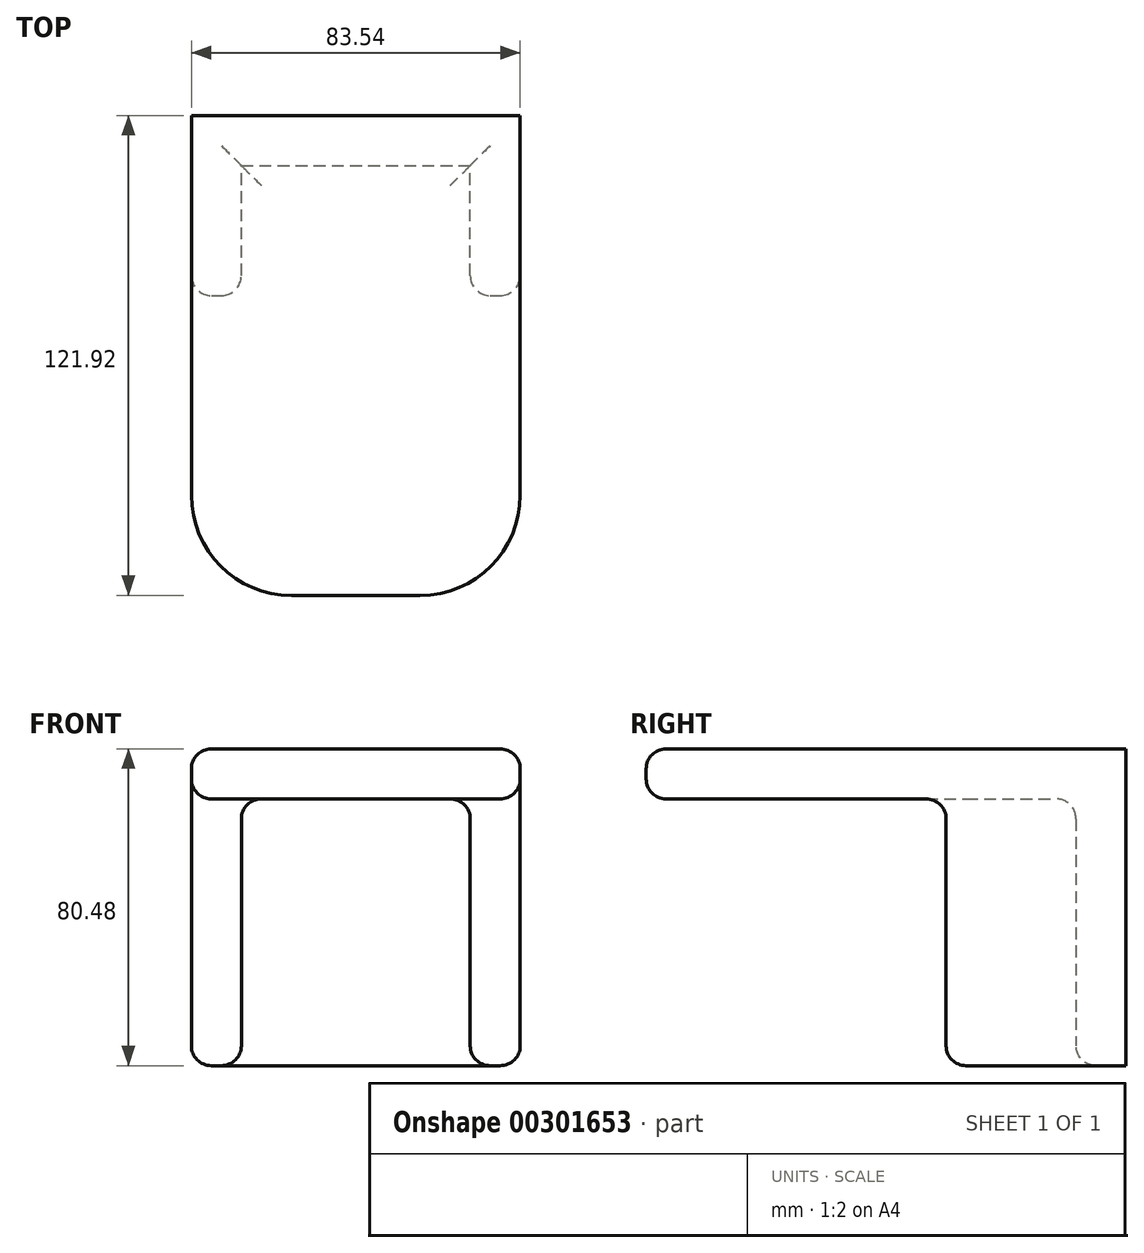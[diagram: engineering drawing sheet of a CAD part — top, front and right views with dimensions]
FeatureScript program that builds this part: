
annotation { "Feature Type Name" : "Feature", "Feature Type Description" : "" }
export const myFeature = defineFeature(function(context is Context, id is Id, definition is map)
    precondition{}
    {
        {
            var Q0;
            Q0=qCreatedBy(makeId("Front.planeOp"),FACE);
            var sketch = newSketch(context, id + "F0", { "sketchPlane" : qUnion([Q0])});
            skLineSegment(sketch, "E0.bottom", {"start": v(-42.6, 33.89) * mm, "end": v(40.95, 33.89) * mm});
            skLineSegment(sketch, "E0.top", {"start": v(-42.6, -46.6) * mm, "end": v(40.95, -46.6) * mm});
            skLineSegment(sketch, "E0.left", {"start": v(-42.6, 33.89) * mm, "end": v(-42.6, -46.6) * mm});
            skLineSegment(sketch, "E0.right", {"start": v(40.95, 33.89) * mm, "end": v(40.95, -46.6) * mm});
            skSolve(sketch);
        }
        {
            var Q0;
            Q0=makeQuery(id+"F0.imprint","IMPRINT",FACE,{"disambiguationData":[TD([[makeQuery(id+"F0.imprint","IMPRINT",EDGE,{"derivedFrom":sQuery(id+"F0.wireOp",EDGE,"E0.bottom")}),-1.0]])]});
            extrude(context, id + "F1", {"entities" : qUnion([Q0]), "depth" : 45.72 * mm});
        }
        {
            var Q0;
            Q0=makeQuery(id+"F1.opExtrude","CAP_FACE",FACE,{"disambiguationData":[OSD([sQuery(id+"F0.wireOp",EDGE,"E0.bottom"),sQuery(id+"F0.wireOp",EDGE,"E0.top"),sQuery(id+"F0.wireOp",EDGE,"E0.left"),sQuery(id+"F0.wireOp",EDGE,"E0.right")])],"isStart":false});
            var Q1;
            Q1=makeQuery(id+"F1.opExtrude","SWEPT_FACE",FACE,{"disambiguationData":[OSD([sQuery(id+"F0.wireOp",EDGE,"E0.top")])]});
            shell(context, id + "F2", {"entities" : qUnion([Q0, Q1]), "thickness" : 12.7 * mm});
        }
        {
            var Q0;
            Q0=makeQuery(id+"F1.opExtrude","CAP_FACE",FACE,{"disambiguationData":[OSD([sQuery(id+"F0.wireOp",EDGE,"E0.bottom"),sQuery(id+"F0.wireOp",EDGE,"E0.top"),sQuery(id+"F0.wireOp",EDGE,"E0.left"),sQuery(id+"F0.wireOp",EDGE,"E0.right")])],"isStart":false});
            var sketch = newSketch(context, id + "F3", { "sketchPlane" : qUnion([Q0])});
            skLineSegment(sketch, "E1.bottom", {"start": v(-42.6, 33.89) * mm, "end": v(40.95, 33.89) * mm});
            skLineSegment(sketch, "E1.top", {"start": v(-42.6, 21.19) * mm, "end": v(40.95, 21.19) * mm});
            skLineSegment(sketch, "E1.left", {"start": v(-42.6, 33.89) * mm, "end": v(-42.6, 21.19) * mm});
            skLineSegment(sketch, "E1.right", {"start": v(40.95, 33.89) * mm, "end": v(40.95, 21.19) * mm});
            skSolve(sketch);
        }
        {
            var Q0;
            Q0=makeQuery(id+"F3.imprint","IMPRINT",FACE,{"disambiguationData":[TD([[makeQuery(id+"F3.imprint","IMPRINT",EDGE,{"derivedFrom":sQuery(id+"F3.wireOp",EDGE,"E1.bottom")}),-1.0]])]});
            extrude(context, id + "F4", {"entities" : qUnion([Q0]), "operationType" : NewBodyOperationType.ADD, "depth" : 76.2 * mm});
        }
        {
            var Q0;
            Q0=makeQuery(id+"F4.opExtrude","CAP_EDGE",EDGE,{"disambiguationData":[OSD([sQuery(id+"F3.wireOp",EDGE,"E1.left")])],"isStart":false});
            var Q1;
            Q1=makeQuery(id+"F4.opExtrude","CAP_EDGE",EDGE,{"disambiguationData":[OSD([sQuery(id+"F3.wireOp",EDGE,"E1.right")])],"isStart":false});
            fillet(context, id + "F5", {"entities" : qUnion([Q0, Q1]), "radius" : 25.4 * mm, "tangentPropagation" : true, "allowEdgeOverflow" : false});
        }
        {
            var Q0;
            Q0=makeQuery(id+"F1.opExtrude","CAP_EDGE",EDGE,{"disambiguationData":[OSD([sQuery(id+"F0.wireOp",EDGE,"E0.left")])],"isStart":false});
            var Q1;
            {var subQ0=sQuery(id+"F0.wireOp",EDGE,"E0.left");Q1=makeQuery(id+"F2.opShell","OFFSET_EDGE",EDGE,{"disambiguationData":[OSD([subQ0]),TDD([makeQuery(id+"F1.opExtrude","CAP_EDGE",EDGE,{"disambiguationData":[OSD([subQ0])],"isStart":false})])]});}
            var Q2;
            {var subQ0=sQuery(id+"F0.wireOp",EDGE,"E0.right");Q2=makeQuery(id+"F2.opShell","OFFSET_EDGE",EDGE,{"disambiguationData":[OSD([subQ0]),TDD([makeQuery(id+"F1.opExtrude","CAP_EDGE",EDGE,{"disambiguationData":[OSD([subQ0])],"isStart":false})])]});}
            var Q3;
            Q3=makeQuery(id+"F1.opExtrude","CAP_EDGE",EDGE,{"disambiguationData":[OSD([sQuery(id+"F0.wireOp",EDGE,"E0.right")])],"isStart":false});
            var Q4;
            {var subQ0=sQuery(id+"F0.wireOp",EDGE,"E0.top");Q4=makeQuery(id+"F2.opShell","OFFSET_EDGE",EDGE,{"disambiguationData":[OSD([subQ0]),TDD([makeQuery(id+"F1.opExtrude","CAP_EDGE",EDGE,{"disambiguationData":[OSD([subQ0])],"isStart":true})])]});}
            var Q5;
            Q5=makeQuery(id+"F4.boolean.opBoolean","MERGE",EDGE,{"derivedFrom":[makeQuery(id+"F1.opExtrude","SWEPT_EDGE",EDGE,{"disambiguationData":[OSD([sQuery(id+"F0.wireOp",EDGE,"E0.bottom"),sQuery(id+"F0.wireOp",EDGE,"E0.left")])]}),makeQuery(id+"F4.opExtrude","SWEPT_EDGE",EDGE,{"disambiguationData":[OSD([sQuery(id+"F3.wireOp",EDGE,"E1.bottom"),sQuery(id+"F3.wireOp",EDGE,"E1.left")])]})]});
            var Q6;
            Q6=makeQuery(id+"F2.opShell","OFFSET_EDGE",EDGE,{"disambiguationData":[OSD([sQuery(id+"F0.wireOp",EDGE,"E0.top"),sQuery(id+"F0.wireOp",EDGE,"E0.right")])]});
            var Q7;
            Q7=makeQuery(id+"F1.opExtrude","SWEPT_EDGE",EDGE,{"disambiguationData":[OSD([sQuery(id+"F0.wireOp",EDGE,"E0.top"),sQuery(id+"F0.wireOp",EDGE,"E0.right")])]});
            var Q8;
            Q8=makeQuery(id+"F2.opShell","OFFSET_EDGE",EDGE,{"disambiguationData":[OSD([sQuery(id+"F0.wireOp",EDGE,"E0.top"),sQuery(id+"F0.wireOp",EDGE,"E0.left")])]});
            var Q9;
            Q9=makeQuery(id+"F1.opExtrude","SWEPT_EDGE",EDGE,{"disambiguationData":[OSD([sQuery(id+"F0.wireOp",EDGE,"E0.top"),sQuery(id+"F0.wireOp",EDGE,"E0.left")])]});
            fillet(context, id + "F6", {"entities" : qUnion([Q0, Q1, Q2, Q3, Q4, Q5, Q6, Q7, Q8, Q9]), "radius" : 5.08 * mm, "tangentPropagation" : true, "allowEdgeOverflow" : false});
        }
        {
            var Q0;
            Q0=makeQuery(id+"F4.boolean.opBoolean","MERGE",FACE,{"derivedFrom":[makeQuery(id+"F2.opShell","OFFSET_FACE",FACE,{"disambiguationData":[OSD([sQuery(id+"F0.wireOp",EDGE,"E0.bottom")])]}),makeQuery(id+"F4.opExtrude","SWEPT_FACE",FACE,{"disambiguationData":[OSD([sQuery(id+"F3.wireOp",EDGE,"E1.top")])]})]});
            fillet(context, id + "F7", {"entities" : qUnion([Q0]), "radius" : 5.08 * mm, "tangentPropagation" : true, "allowEdgeOverflow" : false});
        }
        {
            var Q0;
            {var subQ0=sQuery(id+"F0.wireOp",EDGE,"E0.left");Q0=makeQuery(id+"F6.opFillet","BLEND_EDGE",EDGE,{"blendedFrom":[makeQuery(id+"F2.opShell","OFFSET_EDGE",EDGE,{"disambiguationData":[OSD([sQuery(id+"F0.wireOp",EDGE,"E0.top"),subQ0])]}),makeQuery(id+"F2.opShell","OFFSET_EDGE",EDGE,{"disambiguationData":[OSD([subQ0]),TDD([makeQuery(id+"F1.opExtrude","CAP_EDGE",EDGE,{"disambiguationData":[OSD([subQ0])],"isStart":false})])]})],"blendedInto":[]});}
            var Q1;
            {var subQ0=sQuery(id+"F0.wireOp",EDGE,"E0.right");Q1=makeQuery(id+"F6.opFillet","BLEND_EDGE",EDGE,{"blendedFrom":[makeQuery(id+"F1.opExtrude","SWEPT_EDGE",EDGE,{"disambiguationData":[OSD([sQuery(id+"F0.wireOp",EDGE,"E0.top"),subQ0])]}),makeQuery(id+"F1.opExtrude","CAP_EDGE",EDGE,{"disambiguationData":[OSD([subQ0])],"isStart":false})],"blendedInto":[]});}
            var Q2;
            {var subQ0=sQuery(id+"F0.wireOp",EDGE,"E0.left");Q2=makeQuery(id+"F6.opFillet","BLEND_EDGE",EDGE,{"blendedFrom":[makeQuery(id+"F1.opExtrude","SWEPT_EDGE",EDGE,{"disambiguationData":[OSD([sQuery(id+"F0.wireOp",EDGE,"E0.top"),subQ0])]}),makeQuery(id+"F1.opExtrude","CAP_EDGE",EDGE,{"disambiguationData":[OSD([subQ0])],"isStart":false})],"blendedInto":[]});}
            var Q3;
            {var subQ0=sQuery(id+"F0.wireOp",EDGE,"E0.right");Q3=makeQuery(id+"F6.opFillet","BLEND_EDGE",EDGE,{"blendedFrom":[makeQuery(id+"F2.opShell","OFFSET_EDGE",EDGE,{"disambiguationData":[OSD([sQuery(id+"F0.wireOp",EDGE,"E0.top"),subQ0])]}),makeQuery(id+"F2.opShell","OFFSET_EDGE",EDGE,{"disambiguationData":[OSD([subQ0]),TDD([makeQuery(id+"F1.opExtrude","CAP_EDGE",EDGE,{"disambiguationData":[OSD([subQ0])],"isStart":false})])]})],"blendedInto":[]});}
            fillet(context, id + "F8", {"entities" : qUnion([Q0, Q1, Q2, Q3]), "radius" : 5.08 * mm, "tangentPropagation" : true, "allowEdgeOverflow" : false});
        }
    });
